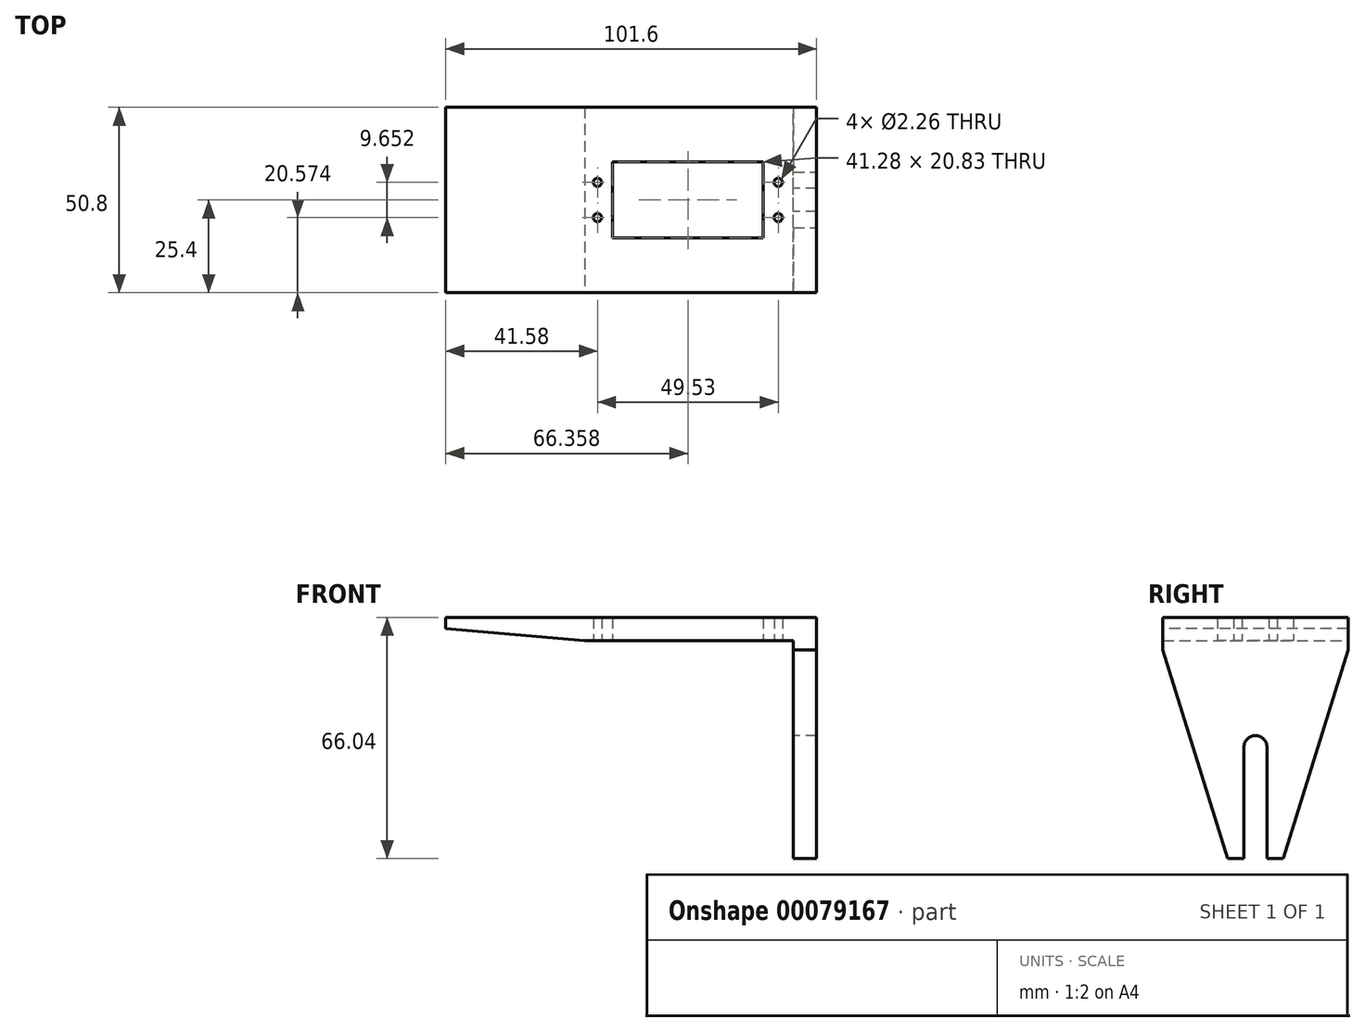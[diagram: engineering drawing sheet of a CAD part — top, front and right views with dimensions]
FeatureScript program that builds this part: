
annotation { "Feature Type Name" : "Feature", "Feature Type Description" : "" }
export const myFeature = defineFeature(function(context is Context, id is Id, definition is map)
    precondition{}
    {
        {
            var Q0;
            Q0=qCreatedBy(makeId("Top.planeOp"),FACE);
            var sketch = newSketch(context, id + "F0", { "sketchPlane" : qUnion([Q0])});
            skLineSegment(sketch, "E0.bottom", {"start": v(0, 0) * mm, "end": v(101.6, 0) * mm});
            skLineSegment(sketch, "E0.top", {"start": v(0, 50.8) * mm, "end": v(101.6, 50.8) * mm});
            skLineSegment(sketch, "E0.left", {"start": v(0, 0) * mm, "end": v(0, 50.8) * mm});
            skLineSegment(sketch, "E0.right", {"start": v(101.6, 0) * mm, "end": v(101.6, 50.8) * mm});
            skLineSegment(sketch, "E1.bottom", {"start": v(45.72, 35.81) * mm, "end": v(87, 35.81) * mm});
            skLineSegment(sketch, "E1.top", {"start": v(45.72, 14.99) * mm, "end": v(87, 14.99) * mm});
            skLineSegment(sketch, "E1.left", {"start": v(45.72, 35.81) * mm, "end": v(45.72, 14.99) * mm});
            skLineSegment(sketch, "E1.right", {"start": v(87, 35.81) * mm, "end": v(87, 14.99) * mm});
            skLineSegment(sketch, "E2.bottom", {"start": v(41.58, 30.23) * mm, "end": v(91.1, 30.23) * mm, "construction": true});
            skLineSegment(sketch, "E2.top", {"start": v(41.58, 20.57) * mm, "end": v(91.1, 20.57) * mm, "construction": true});
            skLineSegment(sketch, "E2.left", {"start": v(41.58, 30.23) * mm, "end": v(41.58, 20.57) * mm, "construction": true});
            skLineSegment(sketch, "E2.right", {"start": v(91.1, 30.23) * mm, "end": v(91.1, 20.57) * mm, "construction": true});
            skCircle(sketch, "E3", {"center": v(41.58, 30.23) * mm, "radius": 1.13 * mm});
            skCircle(sketch, "E4", {"center": v(41.58, 20.57) * mm, "radius": 1.13 * mm});
            skCircle(sketch, "E5", {"center": v(91.1, 30.23) * mm, "radius": 1.13 * mm});
            skCircle(sketch, "E6", {"center": v(91.1, 20.57) * mm, "radius": 1.13 * mm});
            skSolve(sketch);
        }
        {
            var Q0;
            Q0 = qSketchRegion(id + "F0", true);
            extrude(context, id + "F1", {"entities" : qUnion([Q0]), "depth" : 6.35 * mm, "offsetDistance" : 25.4 * mm});
        }
        {
            var Q0;
            Q0=makeQuery(id+"F1.opExtrude","SWEPT_FACE",FACE,{"disambiguationData":[OSD([sQuery(id+"F0.wireOp",EDGE,"E0.bottom")])]});
            var sketch = newSketch(context, id + "F2", { "sketchPlane" : qUnion([Q0])});
            skLineSegment(sketch, "E7", {"start": v(0, 0) * mm, "end": v(0, 3.33) * mm});
            skLineSegment(sketch, "E8", {"start": v(0, 3.33) * mm, "end": v(38.1, 0) * mm});
            skLineSegment(sketch, "E9", {"start": v(38.1, 0) * mm, "end": v(0, 0) * mm});
            skSolve(sketch);
        }
        {
            var Q0;
            Q0 = qSketchRegion(id + "F2", true);
            extrude(context, id + "F3", {"entities" : qUnion([Q0]), "operationType" : NewBodyOperationType.REMOVE, "endBound" : BoundingType.THROUGH_ALL, "oppositeDirection" : true, "depth" : 25.4 * mm, "offsetDistance" : 25.4 * mm});
        }
        {
            var Q0;
            Q0=makeQuery(id+"F1.opExtrude","CAP_FACE",FACE,{"disambiguationData":[OSD([sQuery(id+"F0.wireOp",EDGE,"E0.bottom"),sQuery(id+"F0.wireOp",EDGE,"E0.top"),sQuery(id+"F0.wireOp",EDGE,"E0.left"),sQuery(id+"F0.wireOp",EDGE,"E0.right"),sQuery(id+"F0.wireOp",EDGE,"E1.bottom"),sQuery(id+"F0.wireOp",EDGE,"E1.top"),sQuery(id+"F0.wireOp",EDGE,"E1.left"),sQuery(id+"F0.wireOp",EDGE,"E1.right"),sQuery(id+"F0.wireOp",EDGE,"E3"),sQuery(id+"F0.wireOp",EDGE,"E4"),sQuery(id+"F0.wireOp",EDGE,"E5"),sQuery(id+"F0.wireOp",EDGE,"E6")])],"isStart":true});
            var sketch = newSketch(context, id + "F4", { "sketchPlane" : qUnion([Q0])});
            skLineSegment(sketch, "E10.bottom", {"start": v(101.6, 0) * mm, "end": v(95.25, 0) * mm});
            skLineSegment(sketch, "E10.top", {"start": v(101.6, -50.8) * mm, "end": v(95.25, -50.8) * mm});
            skLineSegment(sketch, "E10.left", {"start": v(101.6, 0) * mm, "end": v(101.6, -50.8) * mm});
            skLineSegment(sketch, "E10.right", {"start": v(95.25, 0) * mm, "end": v(95.25, -50.8) * mm});
            skSolve(sketch);
        }
        {
            var Q0;
            Q0 = qSketchRegion(id + "F4", true);
            extrude(context, id + "F5", {"entities" : qUnion([Q0]), "operationType" : NewBodyOperationType.ADD, "depth" : 59.69 * mm, "offsetDistance" : 25.4 * mm});
        }
        {
            var Q0;
            Q0=makeQuery(id+"F5.opExtrude","SWEPT_FACE",FACE,{"disambiguationData":[OSD([sQuery(id+"F4.wireOp",EDGE,"E10.right")])]});
            var sketch = newSketch(context, id + "F6", { "sketchPlane" : qUnion([Q0])});
            skLineSegment(sketch, "E11.bottom", {"start": v(-28.58, -29.21) * mm, "end": v(-22.23, -29.21) * mm, "construction": true});
            skLineSegment(sketch, "E11.top", {"start": v(-28.58, -59.7) * mm, "end": v(-22.23, -59.7) * mm});
            skLineSegment(sketch, "E11.left", {"start": v(-28.58, -29.21) * mm, "end": v(-28.58, -59.7) * mm});
            skLineSegment(sketch, "E11.right", {"start": v(-22.23, -29.21) * mm, "end": v(-22.23, -59.7) * mm});
            skArc(sketch, "E12", {"start": v(-28.58, -29.21) * mm, "mid": v(-25.4, -26.04) * mm, "end": v(-22.23, -29.21) * mm});
            skLineSegment(sketch, "E13", {"start": v(-25.4, -59.7) * mm, "end": v(-25.4, -29.21) * mm, "construction": true});
            skPoint(sketch, "E13.startSnap0", {"position": v(-25.4, -59.7) * mm});
            skSolve(sketch);
        }
        {
            var Q0;
            Q0 = qSketchRegion(id + "F6", true);
            extrude(context, id + "F7", {"entities" : qUnion([Q0]), "operationType" : NewBodyOperationType.REMOVE, "endBound" : BoundingType.UP_TO_NEXT, "oppositeDirection" : true, "depth" : 25.4 * mm, "offsetDistance" : 25.4 * mm});
        }
        {
            var Q0;
            Q0=makeQuery(id+"F5.boolean.opBoolean","MERGE",FACE,{"derivedFrom":[makeQuery(id+"F1.opExtrude","SWEPT_FACE",FACE,{"disambiguationData":[OSD([sQuery(id+"F0.wireOp",EDGE,"E0.right")])]}),makeQuery(id+"F5.opExtrude","SWEPT_FACE",FACE,{"disambiguationData":[OSD([sQuery(id+"F4.wireOp",EDGE,"E10.left")])]})]});
            var sketch = newSketch(context, id + "F8", { "sketchPlane" : qUnion([Q0])});
            skLineSegment(sketch, "E14", {"start": v(0, -59.7) * mm, "end": v(0, -2.54) * mm});
            skLineSegment(sketch, "E15", {"start": v(0, -2.54) * mm, "end": v(17.78, -59.7) * mm});
            skLineSegment(sketch, "E16", {"start": v(17.78, -59.7) * mm, "end": v(0, -59.7) * mm});
            skLineSegment(sketch, "E17", {"start": v(50.8, -59.7) * mm, "end": v(33.02, -59.7) * mm});
            skLineSegment(sketch, "E18", {"start": v(33.02, -59.7) * mm, "end": v(50.8, -2.54) * mm});
            skLineSegment(sketch, "E19", {"start": v(50.8, -2.54) * mm, "end": v(50.8, -59.7) * mm});
            skLineSegment(sketch, "E20", {"start": v(0, -2.54) * mm, "end": v(50.8, -2.54) * mm});
            skSolve(sketch);
        }
        {
            var Q0;
            Q0 = qSketchRegion(id + "F8", true);
            extrude(context, id + "F9", {"entities" : qUnion([Q0]), "operationType" : NewBodyOperationType.REMOVE, "endBound" : BoundingType.UP_TO_NEXT, "oppositeDirection" : true, "depth" : 25.4 * mm, "offsetDistance" : 25.4 * mm});
        }
    });
